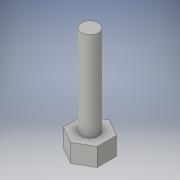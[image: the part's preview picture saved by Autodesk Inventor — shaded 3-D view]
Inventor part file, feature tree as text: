
AUTODESK INVENTOR PART (.ipt)
format: ipt  version: 2016 (Build 200138000, 138)  size: 98,816 bytes
history: native  units: in
note: dims shown in document units (in); Inventor stores cm internally (conversion verified against a paired STEP export)
features: extrude x2, sketch x2
ambient origin geometry x8: Origin, YZ Plane, XZ Plane, XY Plane, X Axis, Y Axis, Z Axis, Center Point
bodies: Solid1 (feature_tree)
feature tree (4):
  extrude  "Extrusion1"  Depth=0.203in TaperAngle=0.0deg
  extrude  "Extrusion2"  Depth=1.0in TaperAngle=0.0deg
  sketch  "Sketch1"  dims[d0=0.375in d1=0.203in d2=0.0in]
  sketch  "Sketch2"  dims[d3=0.19in d4=1.0in d5=0.0in]
